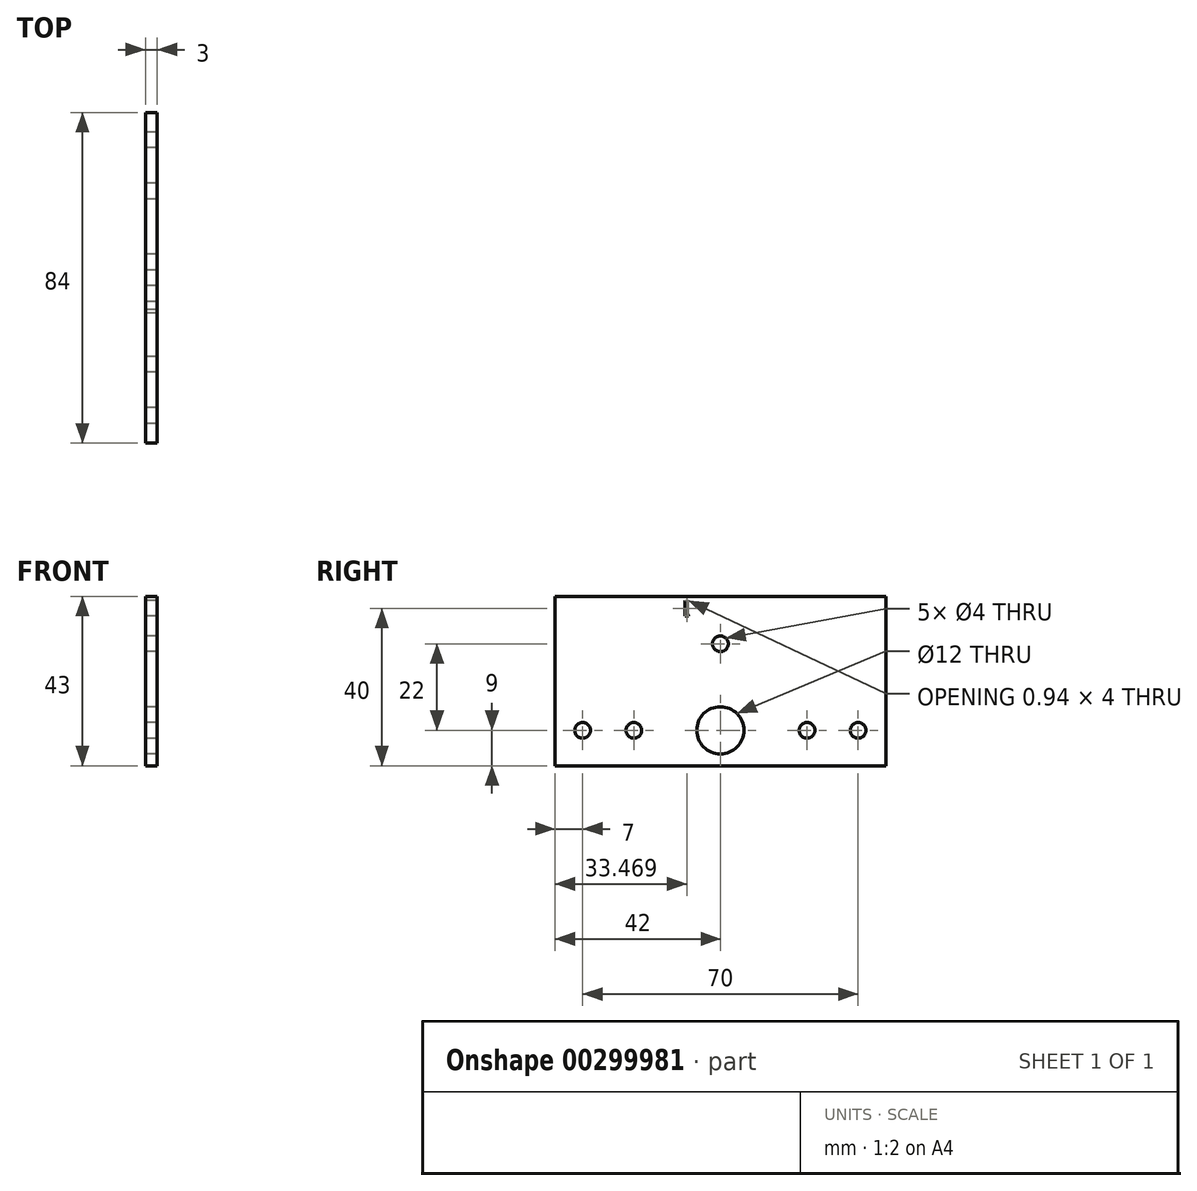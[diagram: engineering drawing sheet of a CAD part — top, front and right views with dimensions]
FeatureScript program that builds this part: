
annotation { "Feature Type Name" : "Feature", "Feature Type Description" : "" }
export const myFeature = defineFeature(function(context is Context, id is Id, definition is map)
    precondition{}
    {
        {
            var Q0;
            Q0=qCreatedBy(makeId("Right.planeOp"),FACE);
            var sketch = newSketch(context, id + "F0", { "sketchPlane" : qUnion([Q0])});
            skLineSegment(sketch, "E0", {"start": v(-42, 0) * mm, "end": v(42, 0) * mm});
            skLineSegment(sketch, "E1", {"start": v(0, 42) * mm, "end": v(0, -42) * mm});
            skCircle(sketch, "E2", {"center": v(0, 33) * mm, "radius": 9 * mm});
            skCircle(sketch, "E3", {"center": v(33, 0) * mm, "radius": 9 * mm});
            skCircle(sketch, "E4", {"center": v(0, -33) * mm, "radius": 9 * mm});
            skCircle(sketch, "E5", {"center": v(-33, 0) * mm, "radius": 9 * mm});
            skLineSegment(sketch, "E6", {"start": v(-33, 0) * mm, "end": v(-33, 9) * mm});
            skLineSegment(sketch, "E7", {"start": v(25, 9) * mm, "end": v(33, 9) * mm});
            skLineSegment(sketch, "E8", {"start": v(33, 0) * mm, "end": v(33, -9) * mm});
            skLineSegment(sketch, "E9", {"start": v(33, -9) * mm, "end": v(25, -9) * mm});
            skLineSegment(sketch, "E10", {"start": v(0, 33) * mm, "end": v(-9, 33) * mm});
            skLineSegment(sketch, "E11", {"start": v(-9, -25) * mm, "end": v(-9, -33) * mm});
            skLineSegment(sketch, "E12", {"start": v(-9, -33) * mm, "end": v(9, -33) * mm});
            skLineSegment(sketch, "E13", {"start": v(9, 25) * mm, "end": v(9, 33) * mm});
            skCircle(sketch, "E14", {"center": v(0, 0) * mm, "radius": 10 * mm});
            skArc(sketch, "E15.filletArc", {"start": v(9, 25) * mm, "mid": v(13.69, 13.69) * mm, "end": v(25, 9) * mm});
            skLineSegment(sketch, "E16", {"start": v(9, -33) * mm, "end": v(9, -25) * mm});
            skArc(sketch, "E17.filletArc", {"start": v(25, -9) * mm, "mid": v(13.69, -13.69) * mm, "end": v(9, -25) * mm});
            skLineSegment(sketch, "E18", {"start": v(-33, 0) * mm, "end": v(-33, -9) * mm});
            skLineSegment(sketch, "E19", {"start": v(-33, -9) * mm, "end": v(-25, -9) * mm});
            skArc(sketch, "E20.filletArc", {"start": v(-9, -25) * mm, "mid": v(-13.69, -13.69) * mm, "end": v(-25, -9) * mm});
            skLineSegment(sketch, "E21", {"start": v(-33, 9) * mm, "end": v(-25, 9) * mm});
            skLineSegment(sketch, "E22", {"start": v(-9, 33) * mm, "end": v(-9, 25) * mm});
            skArc(sketch, "E23.filletArc", {"start": v(-25, 9) * mm, "mid": v(-13.69, 13.69) * mm, "end": v(-9, 25) * mm});
            skCircle(sketch, "E24", {"center": v(-35, 0) * mm, "radius": 2 * mm});
            skCircle(sketch, "E25", {"center": v(-22, 0) * mm, "radius": 2 * mm});
            skCircle(sketch, "E26.1.0", {"center": v(0, -22) * mm, "radius": 2 * mm});
            skCircle(sketch, "E26.1.1", {"center": v(0, -35) * mm, "radius": 2 * mm});
            skCircle(sketch, "E26.2.0", {"center": v(22, 0) * mm, "radius": 2 * mm});
            skCircle(sketch, "E26.2.1", {"center": v(35, 0) * mm, "radius": 2 * mm});
            skCircle(sketch, "E26.3.0", {"center": v(0, 22) * mm, "radius": 2 * mm});
            skCircle(sketch, "E26.3.1", {"center": v(0, 35) * mm, "radius": 2 * mm});
            skPoint(sketch, "E27.firstSnap0", {"position": v(-9, 29) * mm});
            skLineSegment(sketch, "E27.bottom", {"start": v(-42, 29) * mm, "end": v(42, 29) * mm});
            skLineSegment(sketch, "E27.top", {"start": v(-42, -9) * mm, "end": v(42, -9) * mm});
            skLineSegment(sketch, "E27.left", {"start": v(-42, 29) * mm, "end": v(-42, -9) * mm});
            skLineSegment(sketch, "E27.right", {"start": v(42, 29) * mm, "end": v(42, -9) * mm});
            skCircle(sketch, "E28", {"center": v(0, 0) * mm, "radius": 6 * mm});
            skLineSegment(sketch, "E29.top", {"start": v(-42, 34) * mm, "end": v(42, 34) * mm});
            skLineSegment(sketch, "E29.left", {"start": v(-42, 29) * mm, "end": v(-42, 34) * mm});
            skLineSegment(sketch, "E29.right", {"start": v(42, 29) * mm, "end": v(42, 34) * mm});
            skSolve(sketch);
        }
        {
            var Q0;
            {var subQ0=sQuery(id+"F0.wireOp",EDGE,"E27.top");var subQ3=sQuery(id+"F0.wireOp",EDGE,"E27.right");var subQ5=makeQuery(id+"F0.imprint","INTERSECT",VERTEX,{"derivedFrom":[subQ0,subQ3]});Q0=makeQuery(id+"F0.imprint","IMPRINT",FACE,{"disambiguationData":[TD([[makeQuery(id+"F0.imprint","IMPRINT",EDGE,{"disambiguationData":[TD([[subQ5,1.0]])],"derivedFrom":subQ3}),-1.0]])]});}
            var Q1;
            {var subQ0=sQuery(id+"F0.wireOp",EDGE,"E27.top");var subQ3=sQuery(id+"F0.wireOp",EDGE,"E27.left");var subQ5=makeQuery(id+"F0.imprint","INTERSECT",VERTEX,{"derivedFrom":[subQ0,subQ3]});Q1=makeQuery(id+"F0.imprint","IMPRINT",FACE,{"disambiguationData":[TD([[makeQuery(id+"F0.imprint","IMPRINT",EDGE,{"disambiguationData":[TD([[subQ5,1.0]])],"derivedFrom":subQ3}),1.0]])]});}
            var Q2;
            {var subQ4=sQuery(id+"F0.wireOp",EDGE,"E7");Q2=makeQuery(id+"F0.imprint","IMPRINT",FACE,{"disambiguationData":[TD([[makeQuery(id+"F0.imprint","IMPRINT",EDGE,{"derivedFrom":subQ4}),1.0]])]});}
            var Q3;
            {var subQ4=sQuery(id+"F0.wireOp",EDGE,"E21");Q3=makeQuery(id+"F0.imprint","IMPRINT",FACE,{"disambiguationData":[TD([[makeQuery(id+"F0.imprint","IMPRINT",EDGE,{"derivedFrom":subQ4}),1.0]])]});}
            var Q4;
            {var subQ0=sQuery(id+"F0.wireOp",EDGE,"E18");Q4=makeQuery(id+"F0.imprint","IMPRINT",FACE,{"disambiguationData":[TD([[makeQuery(id+"F0.imprint","IMPRINT",EDGE,{"derivedFrom":subQ0}),1.0]])]});}
            var Q5;
            {var subQ0=sQuery(id+"F0.wireOp",EDGE,"E8");Q5=makeQuery(id+"F0.imprint","IMPRINT",FACE,{"disambiguationData":[TD([[makeQuery(id+"F0.imprint","IMPRINT",EDGE,{"derivedFrom":subQ0}),-1.0]])]});}
            var Q6;
            {var subQ5=sQuery(id+"F0.wireOp",EDGE,"E8");Q6=makeQuery(id+"F0.imprint","IMPRINT",FACE,{"disambiguationData":[TD([[makeQuery(id+"F0.imprint","IMPRINT",EDGE,{"derivedFrom":subQ5}),1.0]])]});}
            var Q7;
            {var subQ5=sQuery(id+"F0.wireOp",EDGE,"E6");Q7=makeQuery(id+"F0.imprint","IMPRINT",FACE,{"disambiguationData":[TD([[makeQuery(id+"F0.imprint","IMPRINT",EDGE,{"derivedFrom":subQ5}),1.0]])]});}
            var Q8;
            {var subQ5=sQuery(id+"F0.wireOp",EDGE,"E18");Q8=makeQuery(id+"F0.imprint","IMPRINT",FACE,{"disambiguationData":[TD([[makeQuery(id+"F0.imprint","IMPRINT",EDGE,{"derivedFrom":subQ5}),-1.0]])]});}
            var Q9;
            {var subQ5=sQuery(id+"F0.wireOp",EDGE,"E19");Q9=makeQuery(id+"F0.imprint","IMPRINT",FACE,{"disambiguationData":[TD([[makeQuery(id+"F0.imprint","IMPRINT",EDGE,{"derivedFrom":subQ5}),1.0]])]});}
            var Q10;
            {var subQ0=sQuery(id+"F0.wireOp",EDGE,"E9");Q10=makeQuery(id+"F0.imprint","IMPRINT",FACE,{"disambiguationData":[TD([[makeQuery(id+"F0.imprint","IMPRINT",EDGE,{"derivedFrom":subQ0}),-1.0]])]});}
            var Q11;
            {var subQ2=sQuery(id+"F0.wireOp",EDGE,"E0");var subQ5=sQuery(id+"F0.wireOp",EDGE,"E26.2.1");var subQ6=makeQuery(id+"F0.imprint","INTERSECT",VERTEX,{"derivedFrom":[subQ2,subQ5]});Q11=makeQuery(id+"F0.imprint","IMPRINT",FACE,{"disambiguationData":[TD([[makeQuery(id+"F0.imprint","IMPRINT",EDGE,{"disambiguationData":[TD([[subQ6,-1.0]])],"derivedFrom":subQ2}),1.0]])]});}
            var Q12;
            {var subQ11=sQuery(id+"F0.wireOp",EDGE,"E21");Q12=makeQuery(id+"F0.imprint","IMPRINT",FACE,{"disambiguationData":[TD([[makeQuery(id+"F0.imprint","IMPRINT",EDGE,{"derivedFrom":subQ11}),-1.0]])]});}
            var Q13;
            {var subQ18=sQuery(id+"F0.wireOp",EDGE,"E7");Q13=makeQuery(id+"F0.imprint","IMPRINT",FACE,{"disambiguationData":[TD([[makeQuery(id+"F0.imprint","IMPRINT",EDGE,{"derivedFrom":subQ18}),-1.0]])]});}
            var Q14;
            {var subQ0=sQuery(id+"F0.wireOp",EDGE,"E27.bottom");var subQ1=sQuery(id+"F0.wireOp",EDGE,"E1");var subQ2=makeQuery(id+"F0.imprint","INTERSECT",VERTEX,{"derivedFrom":[subQ1,subQ0]});Q14=makeQuery(id+"F0.imprint","IMPRINT",FACE,{"disambiguationData":[TD([[makeQuery(id+"F0.imprint","IMPRINT",EDGE,{"disambiguationData":[TD([[subQ2,1.0]])],"derivedFrom":subQ0}),-1.0]])]});}
            var Q15;
            {var subQ0=sQuery(id+"F0.wireOp",EDGE,"E27.bottom");var subQ1=sQuery(id+"F0.wireOp",EDGE,"E1");var subQ2=makeQuery(id+"F0.imprint","INTERSECT",VERTEX,{"derivedFrom":[subQ1,subQ0]});Q15=makeQuery(id+"F0.imprint","IMPRINT",FACE,{"disambiguationData":[TD([[makeQuery(id+"F0.imprint","IMPRINT",EDGE,{"disambiguationData":[TD([[subQ2,-1.0]])],"derivedFrom":subQ0}),-1.0]])]});}
            var Q16;
            {var subQ0=sQuery(id+"F0.wireOp",EDGE,"E6");Q16=makeQuery(id+"F0.imprint","IMPRINT",FACE,{"disambiguationData":[TD([[makeQuery(id+"F0.imprint","IMPRINT",EDGE,{"derivedFrom":subQ0}),-1.0]])]});}
            var Q17;
            {var subQ0=sQuery(id+"F0.wireOp",EDGE,"E14");var subQ1=sQuery(id+"F0.wireOp",EDGE,"E0");var subQ2=makeQuery(id+"F0.imprint","INTERSECT",VERTEX,{"disambiguationData":[OD(1.0)],"derivedFrom":[subQ1,subQ0]});Q17=makeQuery(id+"F0.imprint","IMPRINT",FACE,{"disambiguationData":[TD([[makeQuery(id+"F0.imprint","IMPRINT",EDGE,{"disambiguationData":[TD([[subQ2,-1.0]])],"derivedFrom":subQ1}),-1.0]])]});}
            var Q18;
            {var subQ0=sQuery(id+"F0.wireOp",EDGE,"E14");var subQ1=sQuery(id+"F0.wireOp",EDGE,"E0");var subQ2=makeQuery(id+"F0.imprint","INTERSECT",VERTEX,{"disambiguationData":[OD(1.0)],"derivedFrom":[subQ1,subQ0]});Q18=makeQuery(id+"F0.imprint","IMPRINT",FACE,{"disambiguationData":[TD([[makeQuery(id+"F0.imprint","IMPRINT",EDGE,{"disambiguationData":[TD([[subQ2,-1.0]])],"derivedFrom":subQ1}),1.0]])]});}
            var Q19;
            {var subQ0=sQuery(id+"F0.wireOp",EDGE,"E14");var subQ1=sQuery(id+"F0.wireOp",EDGE,"E0");var subQ2=makeQuery(id+"F0.imprint","INTERSECT",VERTEX,{"disambiguationData":[OD(0.0)],"derivedFrom":[subQ1,subQ0]});Q19=makeQuery(id+"F0.imprint","IMPRINT",FACE,{"disambiguationData":[TD([[makeQuery(id+"F0.imprint","IMPRINT",EDGE,{"disambiguationData":[TD([[subQ2,1.0]])],"derivedFrom":subQ1}),1.0]])]});}
            var Q20;
            {var subQ0=sQuery(id+"F0.wireOp",EDGE,"E14");var subQ1=sQuery(id+"F0.wireOp",EDGE,"E0");var subQ2=makeQuery(id+"F0.imprint","INTERSECT",VERTEX,{"disambiguationData":[OD(0.0)],"derivedFrom":[subQ1,subQ0]});Q20=makeQuery(id+"F0.imprint","IMPRINT",FACE,{"disambiguationData":[TD([[makeQuery(id+"F0.imprint","IMPRINT",EDGE,{"disambiguationData":[TD([[subQ2,1.0]])],"derivedFrom":subQ1}),-1.0]])]});}
            var Q21;
            {var subQ0=sQuery(id+"F0.wireOp",EDGE,"E29.right");Q21=makeQuery(id+"F0.imprint","IMPRINT",FACE,{"disambiguationData":[TD([[makeQuery(id+"F0.imprint","IMPRINT",EDGE,{"derivedFrom":subQ0}),1.0]])]});}
            var Q22;
            {var subQ0=sQuery(id+"F0.wireOp",EDGE,"E27.bottom");var subQ1=sQuery(id+"F0.wireOp",EDGE,"E1");var subQ2=makeQuery(id+"F0.imprint","INTERSECT",VERTEX,{"derivedFrom":[subQ1,subQ0]});Q22=makeQuery(id+"F0.imprint","IMPRINT",FACE,{"disambiguationData":[TD([[makeQuery(id+"F0.imprint","IMPRINT",EDGE,{"disambiguationData":[TD([[subQ2,-1.0]])],"derivedFrom":subQ0}),-1.0]])]});}
            var Q23;
            {var subQ0=sQuery(id+"F0.wireOp",EDGE,"E27.bottom");var subQ3=sQuery(id+"F0.wireOp",EDGE,"E2");var subQ5=makeQuery(id+"F0.imprint","INTERSECT",VERTEX,{"disambiguationData":[OD(0.0)],"derivedFrom":[subQ3,subQ0]});Q23=makeQuery(id+"F0.imprint","IMPRINT",FACE,{"disambiguationData":[TD([[makeQuery(id+"F0.imprint","IMPRINT",EDGE,{"disambiguationData":[TD([[subQ5,-1.0]])],"derivedFrom":subQ0}),-1.0]])]});}
            var Q24;
            {var subQ5=sQuery(id+"F0.wireOp",EDGE,"E2");var subQ6=makeQuery(id+"F0.imprint","INTERSECT",VERTEX,{"derivedFrom":[subQ5,sQuery(id+"F0.wireOp",EDGE,"E13")]});Q24=makeQuery(id+"F0.imprint","IMPRINT",FACE,{"disambiguationData":[TD([[makeQuery(id+"F0.imprint","IMPRINT",EDGE,{"disambiguationData":[TD([[subQ6,1.0]])],"derivedFrom":subQ5}),1.0]])]});}
            var Q25;
            {var subQ0=sQuery(id+"F0.wireOp",EDGE,"E10");Q25=makeQuery(id+"F0.imprint","IMPRINT",FACE,{"disambiguationData":[TD([[makeQuery(id+"F0.imprint","IMPRINT",EDGE,{"derivedFrom":subQ0}),1.0]])]});}
            var Q26;
            {var subQ0=sQuery(id+"F0.wireOp",EDGE,"E29.left");Q26=makeQuery(id+"F0.imprint","IMPRINT",FACE,{"disambiguationData":[TD([[makeQuery(id+"F0.imprint","IMPRINT",EDGE,{"derivedFrom":subQ0}),-1.0]])]});}
            var Q27;
            {var subQ0=sQuery(id+"F0.wireOp",EDGE,"E10");Q27=makeQuery(id+"F0.imprint","IMPRINT",FACE,{"disambiguationData":[TD([[makeQuery(id+"F0.imprint","IMPRINT",EDGE,{"derivedFrom":subQ0}),-1.0]])]});}
            var Q28;
            {var subQ1=sQuery(id+"F0.wireOp",EDGE,"E2");var subQ3=sQuery(id+"F0.wireOp",EDGE,"E27.bottom");var subQ4=makeQuery(id+"F0.imprint","INTERSECT",VERTEX,{"disambiguationData":[OD(0.0)],"derivedFrom":[subQ1,subQ3]});Q28=makeQuery(id+"F0.imprint","IMPRINT",FACE,{"disambiguationData":[TD([[makeQuery(id+"F0.imprint","IMPRINT",EDGE,{"disambiguationData":[TD([[subQ4,1.0]])],"derivedFrom":subQ3}),1.0]])]});}
            var Q29;
            {var subQ0=sQuery(id+"F0.wireOp",EDGE,"E13");var subQ1=sQuery(id+"F0.wireOp",EDGE,"E2");var subQ2=makeQuery(id+"F0.imprint","INTERSECT",VERTEX,{"derivedFrom":[subQ1,subQ0]});Q29=makeQuery(id+"F0.imprint","IMPRINT",FACE,{"disambiguationData":[TD([[makeQuery(id+"F0.imprint","IMPRINT",EDGE,{"disambiguationData":[TD([[subQ2,1.0]])],"derivedFrom":subQ1}),-1.0]])]});}
            var Q30;
            {var subQ1=sQuery(id+"F0.wireOp",EDGE,"E1");var subQ3=sQuery(id+"F0.wireOp",EDGE,"E29.top");var subQ4=makeQuery(id+"F0.imprint","INTERSECT",VERTEX,{"derivedFrom":[subQ1,subQ3]});Q30=makeQuery(id+"F0.imprint","IMPRINT",FACE,{"disambiguationData":[TD([[makeQuery(id+"F0.imprint","IMPRINT",EDGE,{"disambiguationData":[TD([[subQ4,1.0]])],"derivedFrom":subQ3}),-1.0]])]});}
            var Q31;
            {var subQ1=sQuery(id+"F0.wireOp",EDGE,"E1");var subQ3=sQuery(id+"F0.wireOp",EDGE,"E29.top");var subQ4=makeQuery(id+"F0.imprint","INTERSECT",VERTEX,{"derivedFrom":[subQ1,subQ3]});Q31=makeQuery(id+"F0.imprint","IMPRINT",FACE,{"disambiguationData":[TD([[makeQuery(id+"F0.imprint","IMPRINT",EDGE,{"disambiguationData":[TD([[subQ4,-1.0]])],"derivedFrom":subQ3}),-1.0]])]});}
            extrude(context, id + "F1", {"entities" : qUnion([Q0, Q1, Q2, Q3, Q4, Q5, Q6, Q7, Q8, Q9, Q10, Q11, Q12, Q13, Q14, Q15, Q16, Q17, Q18, Q19, Q20, Q21, Q22, Q23, Q24, Q25, Q26, Q27, Q28, Q29, Q30, Q31]), "depth" : 3 * mm, "offsetDistance" : 25 * mm});
        }
    });
